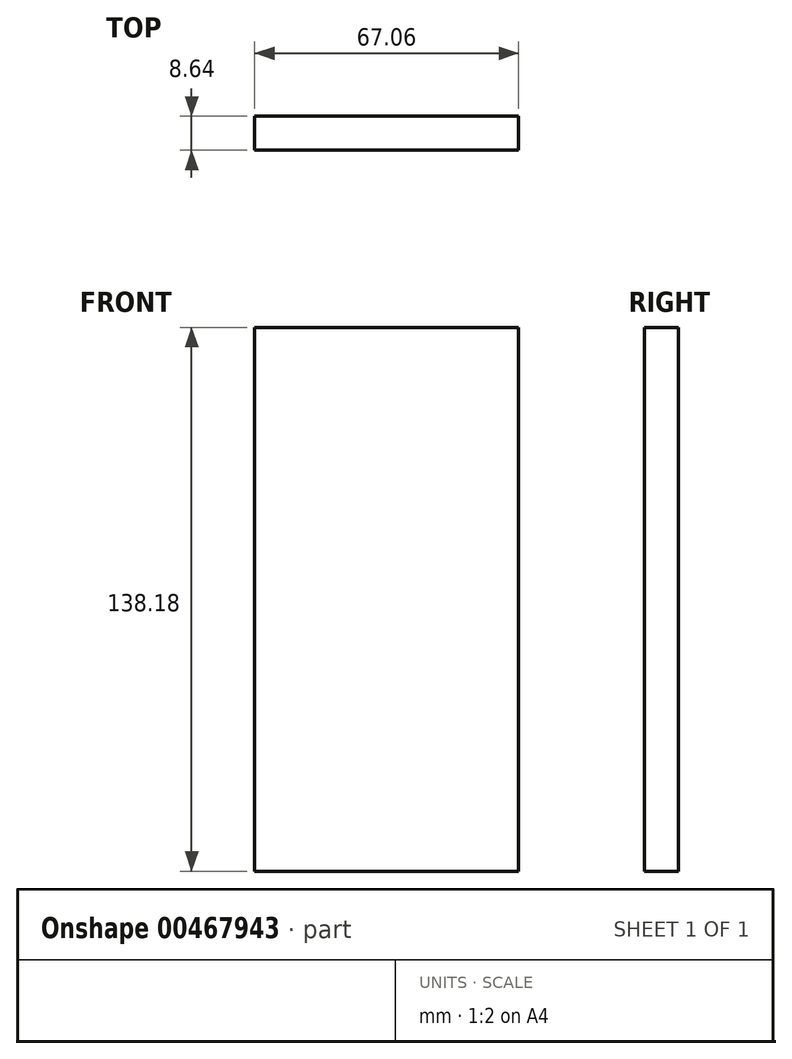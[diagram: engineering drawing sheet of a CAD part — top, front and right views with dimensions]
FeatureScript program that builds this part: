
annotation { "Feature Type Name" : "Feature", "Feature Type Description" : "" }
export const myFeature = defineFeature(function(context is Context, id is Id, definition is map)
    precondition{}
    {
        {
            var Q0;
            Q0=qCreatedBy(makeId("Front.planeOp"),FACE);
            var sketch = newSketch(context, id + "F0", { "sketchPlane" : qUnion([Q0])});
            skLineSegment(sketch, "E0.bottom", {"start": v(-33.53, 69.09) * mm, "end": v(33.53, 69.09) * mm});
            skLineSegment(sketch, "E0.top", {"start": v(-33.53, -69.09) * mm, "end": v(33.53, -69.09) * mm});
            skLineSegment(sketch, "E0.left", {"start": v(-33.53, 69.09) * mm, "end": v(-33.53, -69.09) * mm});
            skLineSegment(sketch, "E0.right", {"start": v(33.53, 69.09) * mm, "end": v(33.53, -69.09) * mm});
            skLineSegment(sketch, "E1", {"start": v(0, 69.09) * mm, "end": v(0, -69.09) * mm, "construction": true});
            skLineSegment(sketch, "E2", {"start": v(-33.53, 0) * mm, "end": v(33.53, 0) * mm, "construction": true});
            skSolve(sketch);
        }
        {
            var Q0;
            Q0=makeQuery(id+"F0.imprint","IMPRINT",FACE,{"disambiguationData":[TD([[makeQuery(id+"F0.imprint","IMPRINT",EDGE,{"derivedFrom":sQuery(id+"F0.wireOp",EDGE,"E0.bottom")}),-1.0]])]});
            extrude(context, id + "F1", {"entities" : qUnion([Q0]), "depth" : 8.64 * mm});
        }
    });
